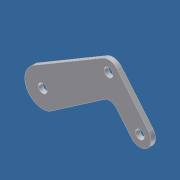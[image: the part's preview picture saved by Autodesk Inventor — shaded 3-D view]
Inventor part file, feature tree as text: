
AUTODESK INVENTOR PART (.ipt)
format: ipt  version: unknown  size: 190,464 bytes
history: native  units: in
note: dims shown in document units (in); Inventor stores cm internally (conversion verified against a paired STEP export)
features: extrude x1, sketch x1
ambient origin geometry x8: Origin, YZ Plane, XZ Plane, XY Plane, X Axis, Y Axis, Z Axis, Center Point
bodies: Solid1 (feature_tree)
feature tree (2):
  extrude  "Extrusion1"  Depth=0.625in
  sketch  "Sketch1"  dims[d0=1.0in d1=0.625in d2=2.25in d3=0.625in d4=1.375in d6=0.25in d7=0.25in d8=0.25in d9=0.25in d10=0.125in d11=0.0in]
